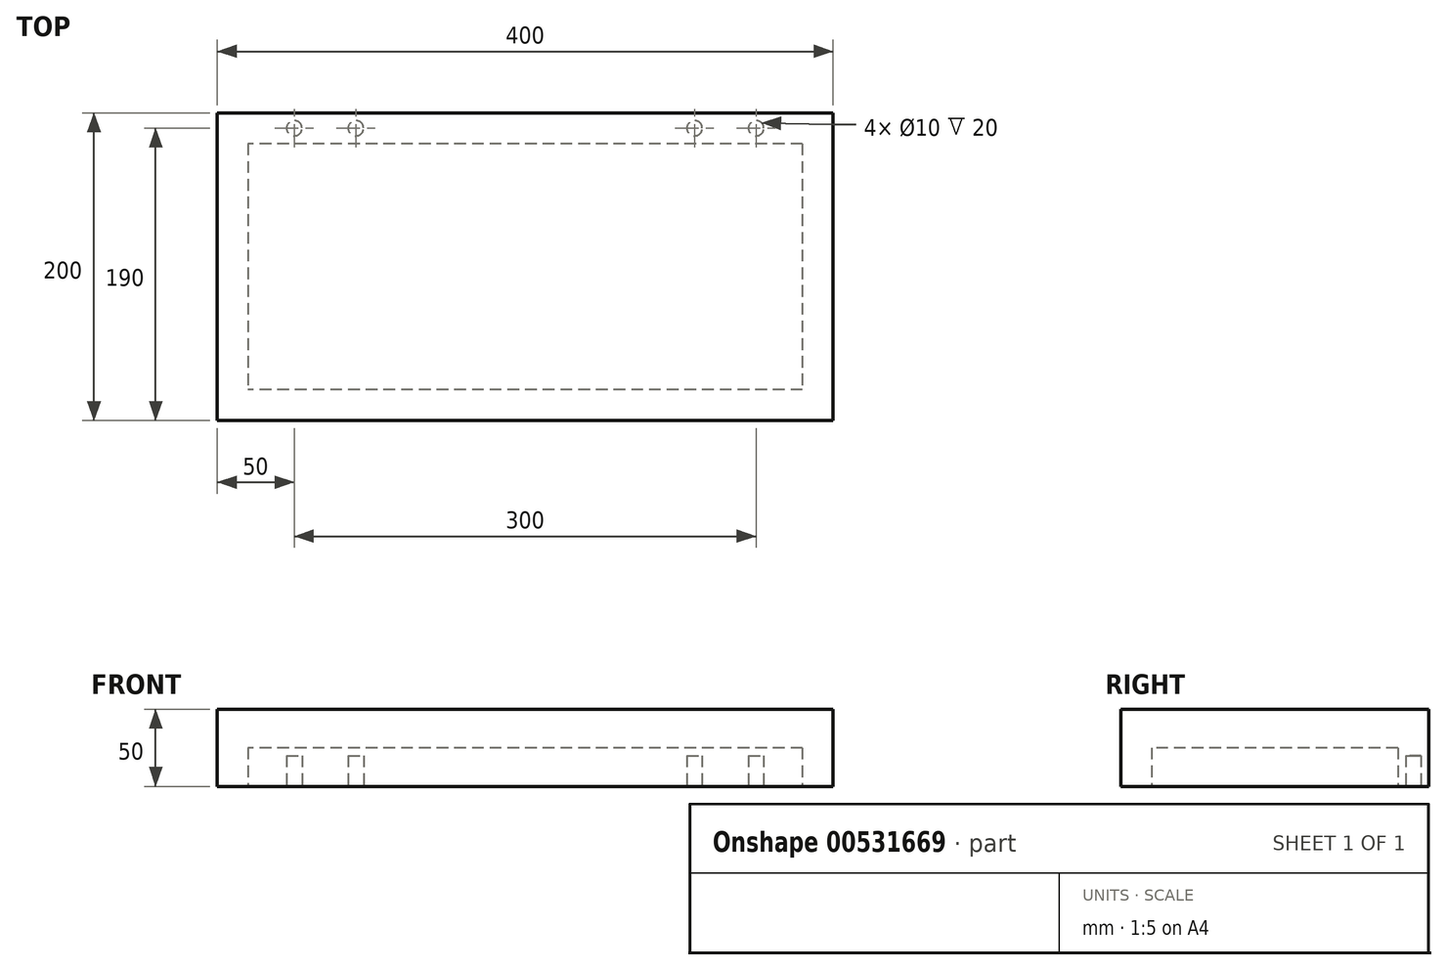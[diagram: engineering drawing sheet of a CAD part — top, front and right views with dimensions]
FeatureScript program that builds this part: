
annotation { "Feature Type Name" : "Feature", "Feature Type Description" : "" }
export const myFeature = defineFeature(function(context is Context, id is Id, definition is map)
    precondition{}
    {
        {
            var Q0;
            Q0=qCreatedBy(makeId("Top.planeOp"),FACE);
            var sketch = newSketch(context, id + "F0", { "sketchPlane" : qUnion([Q0])});
            skLineSegment(sketch, "E0.bottom", {"start": v(200, -100) * mm, "end": v(-200, -100) * mm});
            skLineSegment(sketch, "E0.top", {"start": v(200, 100) * mm, "end": v(-200, 100) * mm});
            skLineSegment(sketch, "E0.left", {"start": v(200, -100) * mm, "end": v(200, 100) * mm});
            skLineSegment(sketch, "E0.right", {"start": v(-200, -100) * mm, "end": v(-200, 100) * mm});
            skPoint(sketch, "E0.middle", {"position": v(0, 0) * mm});
            skSolve(sketch);
        }
        {
            var Q0;
            Q0=qSketchRegion(id+"F0",true);
            extrude(context, id + "F1", {"entities" : qUnion([Q0]), "depth" : 50 * mm, "offsetDistance" : 25 * mm});
        }
        {
            var Q0;
            Q0=makeQuery(id+"F1.opExtrude","CAP_FACE",FACE,{"disambiguationData":[OSD([sQuery(id+"F0.wireOp",EDGE,"E0.bottom"),sQuery(id+"F0.wireOp",EDGE,"E0.top"),sQuery(id+"F0.wireOp",EDGE,"E0.left"),sQuery(id+"F0.wireOp",EDGE,"E0.right")])],"isStart":true});
            var sketch = newSketch(context, id + "F2", { "sketchPlane" : qUnion([Q0])});
            skLineSegment(sketch, "E1.bottom", {"start": v(180, -80) * mm, "end": v(-180, -80) * mm});
            skLineSegment(sketch, "E1.top", {"start": v(180, 80) * mm, "end": v(-180, 80) * mm});
            skLineSegment(sketch, "E1.left", {"start": v(180, -80) * mm, "end": v(180, 80) * mm});
            skLineSegment(sketch, "E1.right", {"start": v(-180, -80) * mm, "end": v(-180, 80) * mm});
            skPoint(sketch, "E1.middle", {"position": v(0, 0) * mm});
            skSolve(sketch);
        }
        {
            var Q0;
            Q0=qSketchRegion(id+"F2",true);
            extrude(context, id + "F3", {"entities" : qUnion([Q0]), "operationType" : NewBodyOperationType.REMOVE, "oppositeDirection" : true, "depth" : 25 * mm});
        }
        {
            var Q0;
            Q0=makeQuery(id+"F1.opExtrude","CAP_FACE",FACE,{"disambiguationData":[OSD([sQuery(id+"F0.wireOp",EDGE,"E0.bottom"),sQuery(id+"F0.wireOp",EDGE,"E0.top"),sQuery(id+"F0.wireOp",EDGE,"E0.left"),sQuery(id+"F0.wireOp",EDGE,"E0.right")])],"isStart":true});
            var sketch = newSketch(context, id + "F4", { "sketchPlane" : qUnion([Q0])});
            skCircle(sketch, "E2", {"center": v(-150, -90) * mm, "radius": 5 * mm});
            skCircle(sketch, "E3", {"center": v(-110, -90) * mm, "radius": 5 * mm});
            skLineSegment(sketch, "E4", {"start": v(0, -80) * mm, "end": v(0, -100) * mm, "construction": true});
            skCircle(sketch, "E5.MirrorC", {"center": v(110, -90) * mm, "radius": 5 * mm});
            skCircle(sketch, "E6.MirrorC", {"center": v(150, -90) * mm, "radius": 5 * mm});
            skSolve(sketch);
        }
        {
            var Q0;
            Q0=qSketchRegion(id+"F4",true);
            extrude(context, id + "F5", {"entities" : qUnion([Q0]), "operationType" : NewBodyOperationType.REMOVE, "oppositeDirection" : true, "depth" : 20 * mm});
        }
    });
